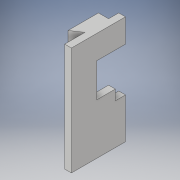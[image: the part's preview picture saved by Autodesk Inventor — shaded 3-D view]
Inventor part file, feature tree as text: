
AUTODESK INVENTOR PART (.ipt)
format: ipt  version: 2019 (Build 230136000, 136)  size: 131,072 bytes
history: native  units: mm
features: extrude x3, sketch x3, projected_geometry x2
ambient origin geometry x8: Origin, YZ Plane, XZ Plane, XY Plane, X Axis, Y Axis, Z Axis, Center Point
bodies: Solid1 (feature_tree)
feature tree (8):
  extrude  "Extrusion1"  Depth=2.0mm
  extrude  "Extrusion2"  Depth=3.0mm
  extrude  "Extrusion3"  Depth=3.0mm
  sketch  "Sketch1"  dims[d0=16.0mm d1=2.0mm]
  sketch  "Sketch2"  dims[d2=6.0mm d3=3.0mm]
  projected_geometry  "Projected Loop1"
  sketch  "Sketch3"  dims[d4=3.0mm d5=9.0mm d6=32.0mm d7=0.0mm d8=25.0mm d9=5.5mm d10=3.0mm d11=0.0mm d12=12.0mm d13=3.0mm d14=3.0mm d15=4.0mm d16=0.0mm]
  projected_geometry  "Projected Loop2"
